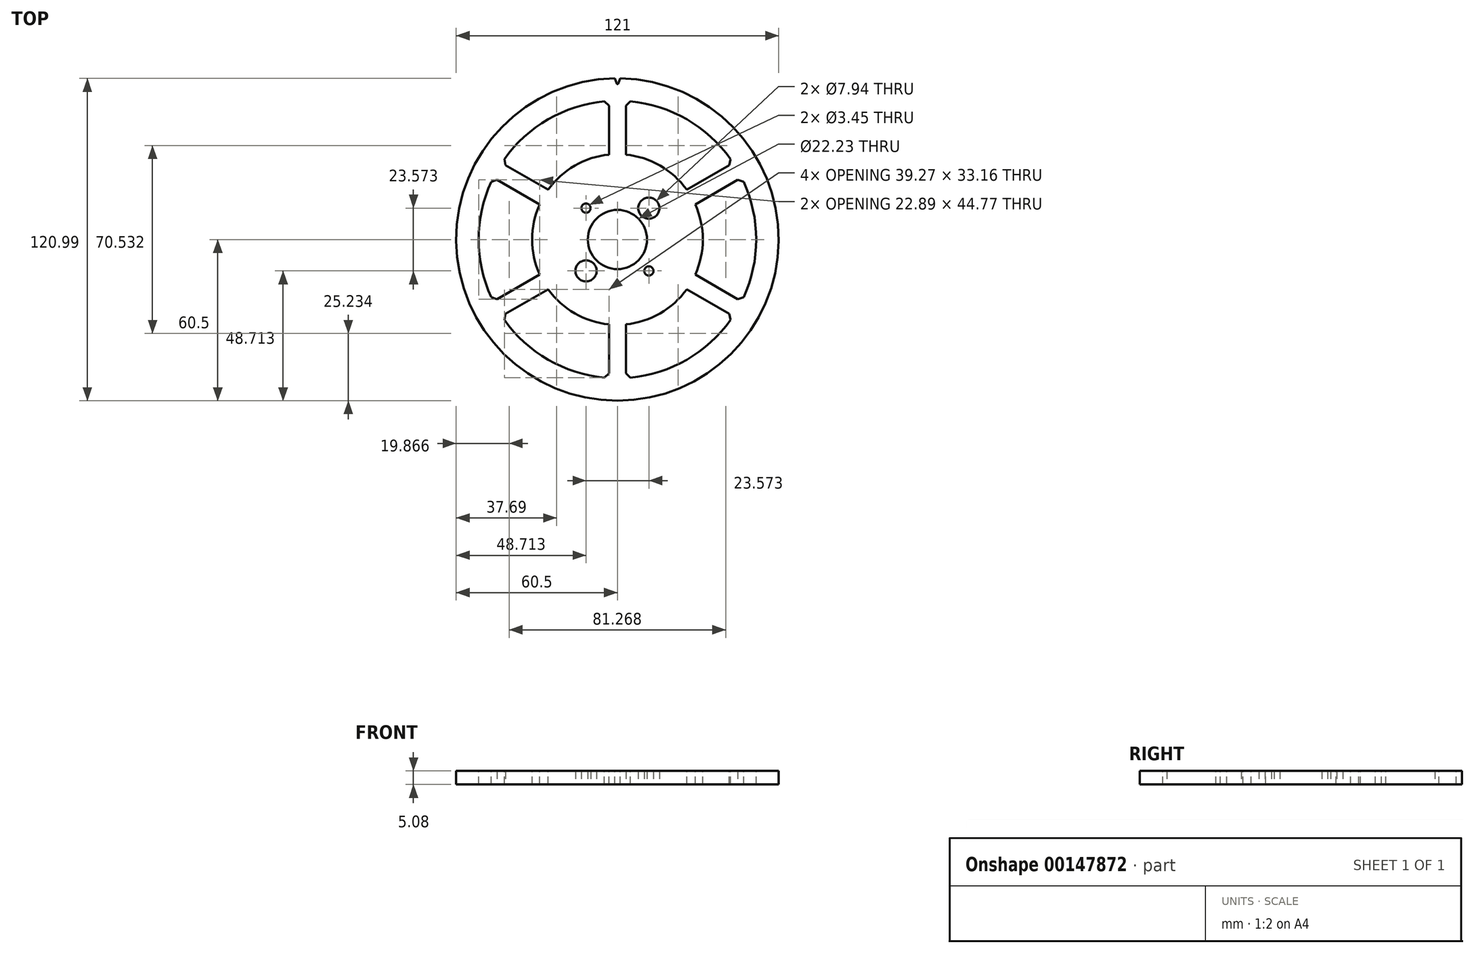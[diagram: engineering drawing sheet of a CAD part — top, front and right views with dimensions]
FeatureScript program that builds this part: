
annotation { "Feature Type Name" : "Feature", "Feature Type Description" : "" }
export const myFeature = defineFeature(function(context is Context, id is Id, definition is map)
    precondition{}
    {
        {
            var Q0;
            Q0=qCreatedBy(makeId("Top.planeOp"),FACE);
            var sketch = newSketch(context, id + "F0", { "sketchPlane" : qUnion([Q0])});
            skCircle(sketch, "E0", {"center": v(0, 0) * mm, "radius": 60.5 * mm});
            skCircle(sketch, "E1", {"center": v(0, 0) * mm, "radius": 11.11 * mm});
            skLineSegment(sketch, "E2.bottom", {"start": v(-11.79, -11.79) * mm, "end": v(11.79, -11.79) * mm, "construction": true});
            skLineSegment(sketch, "E2.top", {"start": v(-11.79, 11.79) * mm, "end": v(11.79, 11.79) * mm, "construction": true});
            skLineSegment(sketch, "E2.left", {"start": v(-11.79, -11.79) * mm, "end": v(-11.79, 11.79) * mm, "construction": true});
            skLineSegment(sketch, "E2.right", {"start": v(11.79, -11.79) * mm, "end": v(11.79, 11.79) * mm, "construction": true});
            skCircle(sketch, "E3", {"center": v(-11.79, -11.79) * mm, "radius": 5.56 * mm, "construction": true});
            skCircle(sketch, "E4", {"center": v(-11.79, -11.79) * mm, "radius": 3.97 * mm});
            skCircle(sketch, "E5", {"center": v(11.79, 11.79) * mm, "radius": 3.97 * mm});
            skCircle(sketch, "E6", {"center": v(11.79, -11.79) * mm, "radius": 1.73 * mm});
            skCircle(sketch, "E7", {"center": v(-11.79, 11.79) * mm, "radius": 1.73 * mm});
            skSolve(sketch);
        }
        {
            var Q0;
            Q0=makeQuery(id+"F0.imprint","IMPRINT",FACE,{"disambiguationData":[TD([[makeQuery(id+"F0.imprint","IMPRINT",EDGE,{"derivedFrom":sQuery(id+"F0.wireOp",EDGE,"d7zeTPih-CRss-xDOh-gPdP-rmPCdwzH7cdN.left")}),1.0]])]});
            var Q1;
            Q1=makeQuery(id+"F0.imprint","IMPRINT",FACE,{"disambiguationData":[TD([[makeQuery(id+"F0.imprint","IMPRINT",EDGE,{"derivedFrom":sQuery(id+"F0.wireOp",EDGE,"E0")}),1.0]])]});
            extrude(context, id + "F1", {"entities" : qUnion([Q0, Q1]), "depth" : 5.08 * mm});
        }
        {
            var Q0;
            Q0=makeQuery(id+"F1.opExtrude","CAP_FACE",FACE,{"disambiguationData":[OSD([sQuery(id+"F0.wireOp",EDGE,"d7zeTPih-CRss-xDOh-gPdP-rmPCdwzH7cdN.left"),sQuery(id+"F0.wireOp",EDGE,"d7zeTPih-CRss-xDOh-gPdP-rmPCdwzH7cdN.right"),sQuery(id+"F0.wireOp",EDGE,"ScfBMfkV-s1yN-Ls9R-SGr5-fEyGpD6zak8e"),sQuery(id+"F0.wireOp",EDGE,"xnxmVwjl-FvSF-m7sj-be2U-u85gZZGoORGZ"),sQuery(id+"F0.wireOp",EDGE,"E0")])],"isStart":false});
            var sketch = newSketch(context, id + "F2", { "sketchPlane" : qUnion([Q0])});
            skLineSegment(sketch, "E8", {"start": v(0, 0) * mm, "end": v(0, 60.5) * mm, "construction": true});
            skLineSegment(sketch, "E9", {"start": v(0, 0) * mm, "end": v(0.66, 60.5) * mm, "construction": true});
            skArc(sketch, "E10", {"start": v(1.02, 60.5) * mm, "mid": v(0, 60.5) * mm, "end": v(-1.02, 60.5) * mm});
            skLineSegment(sketch, "E11", {"start": v(-1.02, 60.5) * mm, "end": v(-0.28, 58.52) * mm});
            skLineSegment(sketch, "E12", {"start": v(1.02, 60.5) * mm, "end": v(0.28, 58.52) * mm});
            skPoint(sketch, "E13", {"position": v(0.65, 59.5) * mm});
            skArc(sketch, "E14", {"start": v(-0.28, 58.52) * mm, "mid": v(0, 58.33) * mm, "end": v(0.28, 58.52) * mm});
            skSolve(sketch);
        }
        {
            var Q0;
            Q0=qSketchRegion(id+"F2",true);
            var Q1;
            Q1=makeQuery(id+"F1.opExtrude","CAP_FACE",FACE,{"disambiguationData":[OSD([sQuery(id+"F0.wireOp",EDGE,"d7zeTPih-CRss-xDOh-gPdP-rmPCdwzH7cdN.left"),sQuery(id+"F0.wireOp",EDGE,"d7zeTPih-CRss-xDOh-gPdP-rmPCdwzH7cdN.right"),sQuery(id+"F0.wireOp",EDGE,"ScfBMfkV-s1yN-Ls9R-SGr5-fEyGpD6zak8e"),sQuery(id+"F0.wireOp",EDGE,"xnxmVwjl-FvSF-m7sj-be2U-u85gZZGoORGZ"),sQuery(id+"F0.wireOp",EDGE,"E0")])],"isStart":true});
            extrude(context, id + "F3", {"entities" : qUnion([Q0]), "operationType" : NewBodyOperationType.REMOVE, "endBound" : BoundingType.UP_TO_SURFACE, "oppositeDirection" : true, "endBoundEntityFace" : qUnion([Q1]), "depth" : 25.4 * mm});
        }
        {
            var Q0;
            Q0=makeQuery(id+"F1.opExtrude","CAP_FACE",FACE,{"disambiguationData":[OSD([sQuery(id+"F0.wireOp",EDGE,"E0"),sQuery(id+"F0.wireOp",EDGE,"E1"),sQuery(id+"F0.wireOp",EDGE,"E4"),sQuery(id+"F0.wireOp",EDGE,"E5"),sQuery(id+"F0.wireOp",EDGE,"E6"),sQuery(id+"F0.wireOp",EDGE,"E7")])],"isStart":false});
            var sketch = newSketch(context, id + "F4", { "sketchPlane" : qUnion([Q0])});
            skLineSegment(sketch, "E15", {"start": v(0, 0) * mm, "end": v(0, 31.87) * mm, "construction": true});
            skLineSegment(sketch, "E16", {"start": v(0, 31.87) * mm, "end": v(3.18, 31.87) * mm, "construction": true});
            skLineSegment(sketch, "E17", {"start": v(3.18, 31.87) * mm, "end": v(3.18, 51.98) * mm});
            skLineSegment(sketch, "E18", {"start": v(3.18, 51.98) * mm, "end": v(0, 51.98) * mm, "construction": true});
            skLineSegment(sketch, "E19", {"start": v(0, 51.98) * mm, "end": v(0, 58.33) * mm, "construction": true});
            skCircle(sketch, "E20", {"center": v(0, 0) * mm, "radius": 58.33 * mm, "construction": true});
            skArc(sketch, "E21", {"start": v(26.01, 18.69) * mm, "mid": v(16.01, 27.74) * mm, "end": v(3.17, 31.87) * mm});
            skLineSegment(sketch, "E22", {"start": v(0, 0) * mm, "end": v(27.6, 15.94) * mm, "construction": true});
            skLineSegment(sketch, "E23", {"start": v(27.6, 15.94) * mm, "end": v(26.01, 18.69) * mm, "construction": true});
            skLineSegment(sketch, "E24", {"start": v(26.01, 18.69) * mm, "end": v(43.43, 28.74) * mm});
            skArc(sketch, "E25", {"start": v(43.43, 28.74) * mm, "mid": v(26.04, 45.1) * mm, "end": v(3.18, 51.98) * mm});
            skSolve(sketch);
        }
        {
            var Q0;
            Q0=qSketchRegion(id+"F4",true);
            var Q1;
            Q1=makeQuery(id+"F1.opExtrude","SWEPT_BODY",BODY,{"disambiguationData":[OSD([sQuery(id+"F0.wireOp",EDGE,"E0"),sQuery(id+"F0.wireOp",EDGE,"E1"),sQuery(id+"F0.wireOp",EDGE,"E4"),sQuery(id+"F0.wireOp",EDGE,"E5"),sQuery(id+"F0.wireOp",EDGE,"E6"),sQuery(id+"F0.wireOp",EDGE,"E7")])]});
            extrude(context, id + "F5", {"entities" : qUnion([Q0]), "operationType" : NewBodyOperationType.REMOVE, "endBound" : BoundingType.UP_TO_BODY, "oppositeDirection" : true, "endBoundEntityBody" : qUnion([Q1]), "depth" : 25.4 * mm});
        }
        {
            var Q0;
            Q0=makeQuery(id+"F5.boolean.opBoolean","COPY",EDGE,{"derivedFrom":makeQuery(id+"F5.opExtrude","SWEPT_EDGE",EDGE,{"disambiguationData":[OSD([sQuery(id+"F4.wireOp",EDGE,"E17"),sQuery(id+"F4.wireOp",EDGE,"E25")])]})});
            var Q1;
            Q1=makeQuery(id+"F5.boolean.opBoolean","COPY",EDGE,{"derivedFrom":makeQuery(id+"F5.opExtrude","SWEPT_EDGE",EDGE,{"disambiguationData":[OSD([sQuery(id+"F4.wireOp",EDGE,"E24"),sQuery(id+"F4.wireOp",EDGE,"E25")])]})});
            chamfer(context, id + "F6", {"entities" : qUnion([Q0, Q1]), "width" : 1.59 * mm, "tangentPropagation" : true});
        }
        {
            var Q0;
            Q0=makeQuery(id+"F6.opChamfer","BLEND_FACE",FACE,{"disambiguationData":[OSD([sQuery(id+"F4.wireOp",EDGE,"E17"),sQuery(id+"F4.wireOp",EDGE,"E21")])]});
            var Q1;
            Q1=makeQuery(id+"F5.boolean.opBoolean","COPY",FACE,{"derivedFrom":makeQuery(id+"F5.opExtrude","SWEPT_FACE",FACE,{"disambiguationData":[OSD([sQuery(id+"F4.wireOp",EDGE,"E21")])]})});
            var Q2;
            Q2=makeQuery(id+"F5.boolean.opBoolean","COPY",FACE,{"derivedFrom":makeQuery(id+"F5.opExtrude","SWEPT_FACE",FACE,{"disambiguationData":[OSD([sQuery(id+"F4.wireOp",EDGE,"E17")])]})});
            var Q3;
            Q3=makeQuery(id+"F6.opChamfer","BLEND_FACE",FACE,{"disambiguationData":[OSD([sQuery(id+"F4.wireOp",EDGE,"E17"),sQuery(id+"F4.wireOp",EDGE,"E25")])]});
            var Q4;
            Q4=makeQuery(id+"F5.boolean.opBoolean","COPY",FACE,{"derivedFrom":makeQuery(id+"F5.opExtrude","SWEPT_FACE",FACE,{"disambiguationData":[OSD([sQuery(id+"F4.wireOp",EDGE,"E25")])]})});
            var Q5;
            Q5=makeQuery(id+"F5.boolean.opBoolean","COPY",FACE,{"derivedFrom":makeQuery(id+"F5.opExtrude","SWEPT_FACE",FACE,{"disambiguationData":[OSD([sQuery(id+"F4.wireOp",EDGE,"E24")])]})});
            var Q6;
            Q6=makeQuery(id+"F6.opChamfer","BLEND_FACE",FACE,{"disambiguationData":[OSD([sQuery(id+"F4.wireOp",EDGE,"E21"),sQuery(id+"F4.wireOp",EDGE,"E24")])]});
            var Q7;
            Q7=makeQuery(id+"F6.opChamfer","BLEND_FACE",FACE,{"disambiguationData":[OSD([sQuery(id+"F4.wireOp",EDGE,"E24"),sQuery(id+"F4.wireOp",EDGE,"E25")])]});
            var Q8;
            Q8=makeQuery(id+"F1.opExtrude","SWEPT_FACE",FACE,{"disambiguationData":[OSD([sQuery(id+"F0.wireOp",EDGE,"E1")])]});
            circularPattern(context, id + "F7", {"patternType" : PatternType.FACE, "faces" : qUnion([Q0, Q1, Q2, Q3, Q4, Q5, Q6, Q7]), "axis" : qUnion([Q8]), "angle" : 60 * degree, "instanceCount" : 6});
        }
    });
